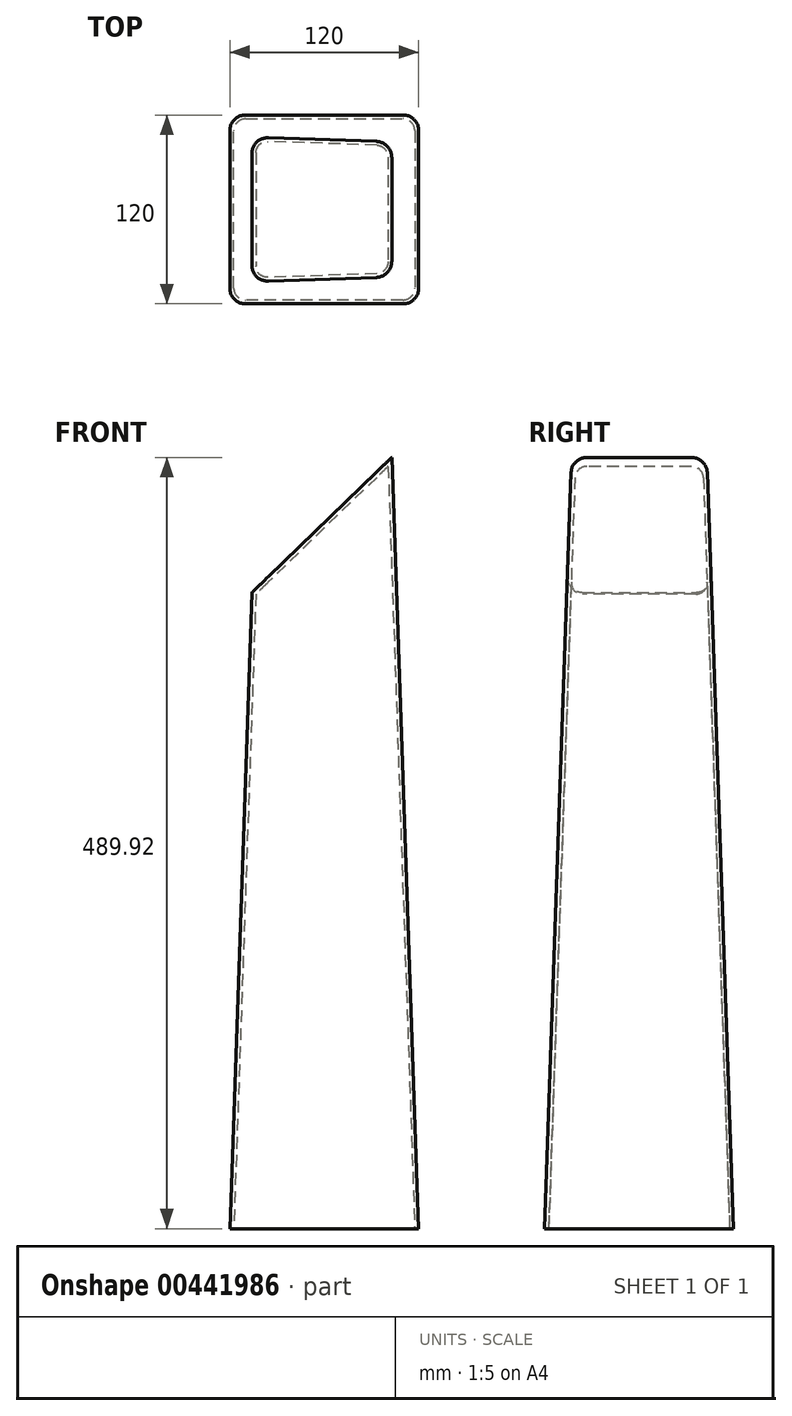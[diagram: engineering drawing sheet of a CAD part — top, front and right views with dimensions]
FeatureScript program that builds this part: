
annotation { "Feature Type Name" : "Feature", "Feature Type Description" : "" }
export const myFeature = defineFeature(function(context is Context, id is Id, definition is map)
    precondition{}
    {
        {
            var Q0;
            Q0=qCreatedBy(makeId("Top.planeOp"),FACE);
            var sketch = newSketch(context, id + "F0", { "sketchPlane" : qUnion([Q0])});
            skLineSegment(sketch, "E0.bottom", {"start": v(0, 0) * mm, "end": v(120, 0) * mm});
            skLineSegment(sketch, "E0.top", {"start": v(0, 120) * mm, "end": v(120, 120) * mm});
            skLineSegment(sketch, "E0.left", {"start": v(0, 0) * mm, "end": v(0, 120) * mm});
            skLineSegment(sketch, "E0.right", {"start": v(120, 0) * mm, "end": v(120, 120) * mm});
            skLineSegment(sketch, "E1", {"start": v(0, 120) * mm, "end": v(120, 0) * mm});
            skLineSegment(sketch, "E2", {"start": v(120, 120) * mm, "end": v(0, 0) * mm});
            skPoint(sketch, "E3", {"position": v(60, 60) * mm});
            skSolve(sketch);
        }
        {
            var Q0;
            Q0=qCreatedBy(makeId("Top.planeOp"),FACE);
            var sketch = newSketch(context, id + "F1", { "sketchPlane" : qUnion([Q0])});
            skPoint(sketch, "E4", {"position": v(59.92, 57.62) * mm});
            skSolve(sketch);
        }
        {
            var Q0;
            Q0=qSketchRegion(id+"F1",true);
            var Q1;
            {var subQ0=sQuery(id+"F0.wireOp",EDGE,"E0.top");Q1=makeQuery(id+"F0.imprint","IMPRINT",FACE,{"disambiguationData":[TD([[makeQuery(id+"F0.imprint","IMPRINT",EDGE,{"derivedFrom":subQ0}),-1.0]])]});}
            var Q2;
            {var subQ0=sQuery(id+"F0.wireOp",EDGE,"E0.right");Q2=makeQuery(id+"F0.imprint","IMPRINT",FACE,{"disambiguationData":[TD([[makeQuery(id+"F0.imprint","IMPRINT",EDGE,{"derivedFrom":subQ0}),1.0]])]});}
            var Q3;
            {var subQ0=sQuery(id+"F0.wireOp",EDGE,"E0.bottom");Q3=makeQuery(id+"F0.imprint","IMPRINT",FACE,{"disambiguationData":[TD([[makeQuery(id+"F0.imprint","IMPRINT",EDGE,{"derivedFrom":subQ0}),1.0]])]});}
            var Q4;
            {var subQ0=sQuery(id+"F0.wireOp",EDGE,"E0.left");Q4=makeQuery(id+"F0.imprint","IMPRINT",FACE,{"disambiguationData":[TD([[makeQuery(id+"F0.imprint","IMPRINT",EDGE,{"derivedFrom":subQ0}),-1.0]])]});}
            extrude(context, id + "F2", {"entities" : qUnion([Q0, Q1, Q2, Q3, Q4]), "depth" : 520 * mm, "hasDraft" : true, "draftAngle" : 2 * degree, "draftPullDirection" : true});
        }
        {
            var Q0;
            Q0=makeQuery(id+"F2.opExtrude","CAP_EDGE",EDGE,{"disambiguationData":[OSD([sQuery(id+"F0.wireOp",EDGE,"E0.left")])],"isStart":false});
            chamfer(context, id + "F3", {"entities" : qUnion([Q0]), "width" : 120 * mm, "tangentPropagation" : true});
        }
        {
            var Q0;
            Q0=makeQuery(id+"F2.opExtrude","SWEPT_EDGE",EDGE,{"disambiguationData":[OSD([sQuery(id+"F0.wireOp",EDGE,"E0.bottom"),sQuery(id+"F0.wireOp",EDGE,"E0.left"),sQuery(id+"F0.wireOp",EDGE,"E2")])]});
            var Q1;
            Q1=makeQuery(id+"F2.opExtrude","SWEPT_EDGE",EDGE,{"disambiguationData":[OSD([sQuery(id+"F0.wireOp",EDGE,"E0.top"),sQuery(id+"F0.wireOp",EDGE,"E0.left"),sQuery(id+"F0.wireOp",EDGE,"E1")])]});
            var Q2;
            Q2=makeQuery(id+"F2.opExtrude","SWEPT_EDGE",EDGE,{"disambiguationData":[OSD([sQuery(id+"F0.wireOp",EDGE,"E0.bottom"),sQuery(id+"F0.wireOp",EDGE,"E0.right"),sQuery(id+"F0.wireOp",EDGE,"E1")])]});
            var Q3;
            Q3=makeQuery(id+"F2.opExtrude","SWEPT_EDGE",EDGE,{"disambiguationData":[OSD([sQuery(id+"F0.wireOp",EDGE,"E0.top"),sQuery(id+"F0.wireOp",EDGE,"E0.right"),sQuery(id+"F0.wireOp",EDGE,"E2")])]});
            fillet(context, id + "F4", {"entities" : qUnion([Q0, Q1, Q2, Q3]), "radius" : 10 * mm, "tangentPropagation" : true, "allowEdgeOverflow" : false});
        }
        {
            var Q0;
            Q0=makeQuery(id+"F2.opExtrude","CAP_FACE",FACE,{"disambiguationData":[OSD([sQuery(id+"F0.wireOp",EDGE,"E0.bottom"),sQuery(id+"F0.wireOp",EDGE,"E0.top"),sQuery(id+"F0.wireOp",EDGE,"E0.left"),sQuery(id+"F0.wireOp",EDGE,"E0.right")])],"isStart":true});
            shell(context, id + "F5", {"entities" : qUnion([Q0]), "thickness" : 2.5 * mm});
        }
    });
